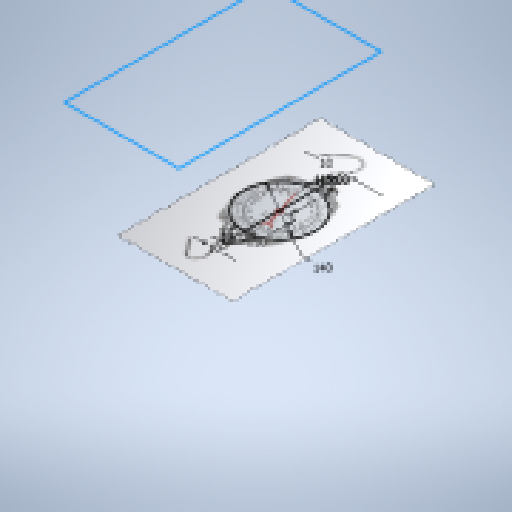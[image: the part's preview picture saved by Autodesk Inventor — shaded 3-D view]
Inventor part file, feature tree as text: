
AUTODESK INVENTOR PART (.ipt)
format: ipt  version: 2025 (Build 290162010, 162A)  size: 399,872 bytes
history: native  units: mm
features: sketch x2, extrude x2, other x2
ambient origin geometry x8: Origin, YZ Plane, XZ Plane, XY Plane, X Axis, Y Axis, Z Axis, Center Point
bodies: Volumenkörper1 (feature_tree)
feature tree (6):
  sketch  "Skizze2"  dims[d3=19.198622mm d4=19.198622mm]
  extrude  "Extrusion1"  Depth=19.198622mm
  extrude  "Extrusion2"  Depth=7.0mm
  sketch  "Skizze3"  dims[d5=110.0mm d8=140.0mm d9=110.0mm d10=19.198622mm d11=19.198622mm d12=10.0mm d13=10.0mm d22=20.0mm d23=0.0mm d24=7.0mm d25=0.0mm]
  other  "Bild1"
  other  "Bild2"
